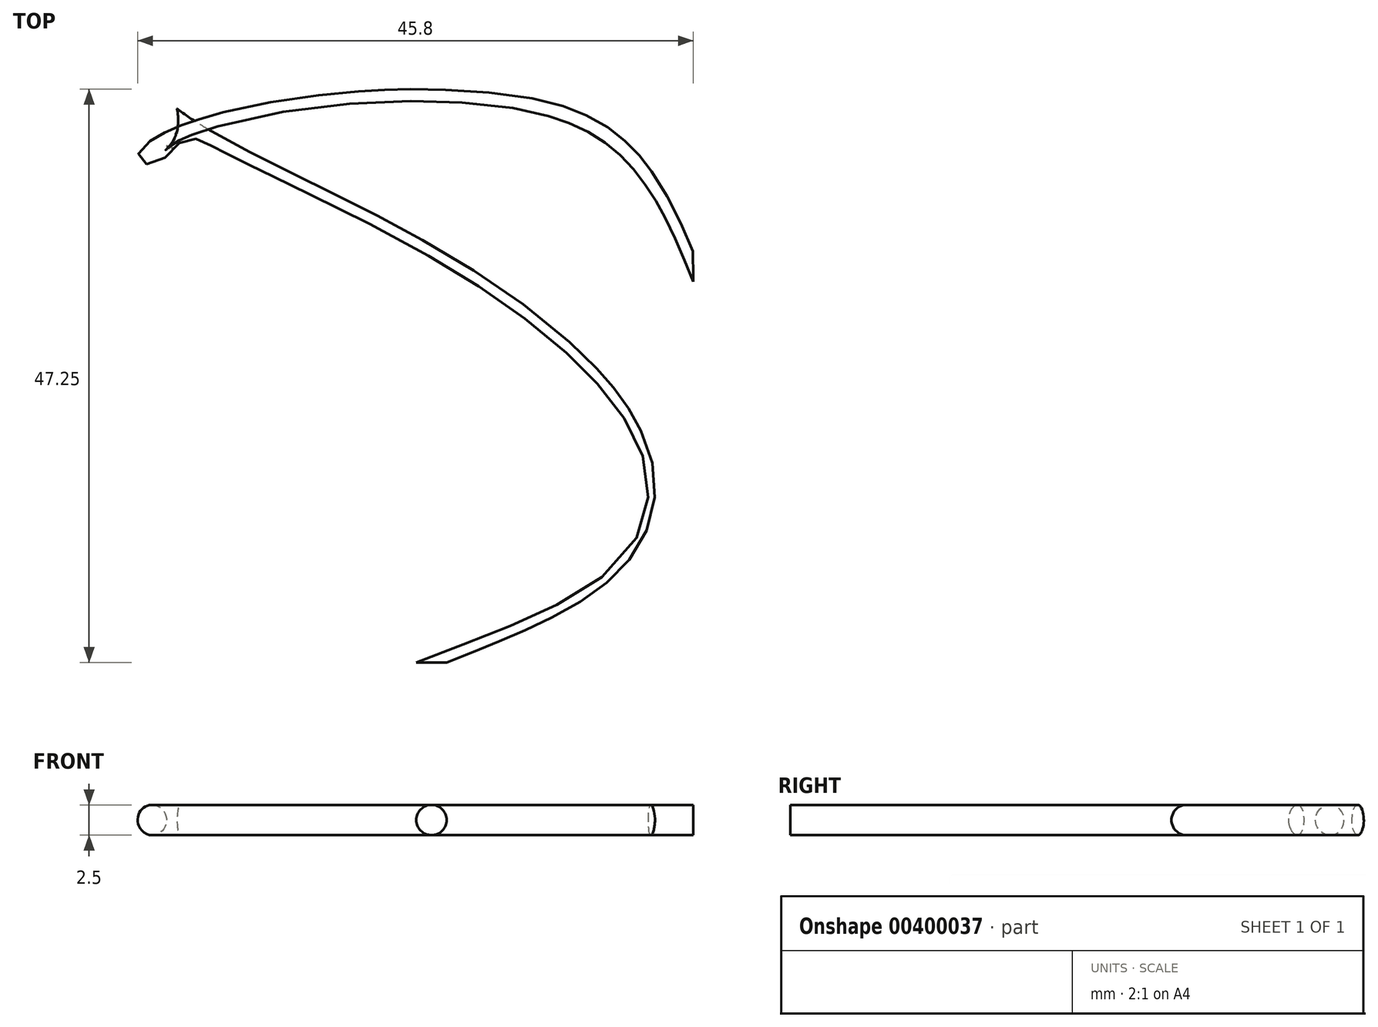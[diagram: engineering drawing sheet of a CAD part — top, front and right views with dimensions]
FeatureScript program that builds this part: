
annotation { "Feature Type Name" : "Feature", "Feature Type Description" : "" }
export const myFeature = defineFeature(function(context is Context, id is Id, definition is map)
    precondition{}
    {
        {
            var Q0;
            Q0=qCreatedBy(makeId("Front.planeOp"),FACE);
            var sketch = newSketch(context, id + "F0", { "sketchPlane" : qUnion([Q0])});
            skCircle(sketch, "E0", {"center": v(-33.05, 45.34) * mm, "radius": 1.25 * mm});
            skSolve(sketch);
        }
        {
            var Q0;
            Q0=qCreatedBy(makeId("Top.planeOp"),FACE);
            var sketch = newSketch(context, id + "F1", { "sketchPlane" : qUnion([Q0])});
            skFitSpline(sketch, "E1", {"points": [v(-33.2, 4.7) * mm, v(-19.6, 13.6) * mm, v(-36.28, 30.61) * mm, v(-58.63, 45.19) * mm, v(-22.03, 49.72) * mm, v(-6.8, 32.88) * mm], "startDerivative": vector(119.48, 46.6) * mm, "endDerivative": vector(45.4, -110.5) * mm});
            skSolve(sketch);
        }
        {
            var Q0;
            Q0=makeQuery(id+"F0.imprint","IMPRINT",FACE,{"disambiguationData":[TD([[makeQuery(id+"F0.imprint","IMPRINT",EDGE,{"derivedFrom":sQuery(id+"F0.wireOp",EDGE,"E0")}),1.0]])]});
            var Q1;
            Q1=sQuery(id+"F1.wireOp",EDGE,"E1");
            sweep(context, id + "F2", {"profiles" : qUnion([Q0]), "path" : qUnion([Q1])});
        }
    });
